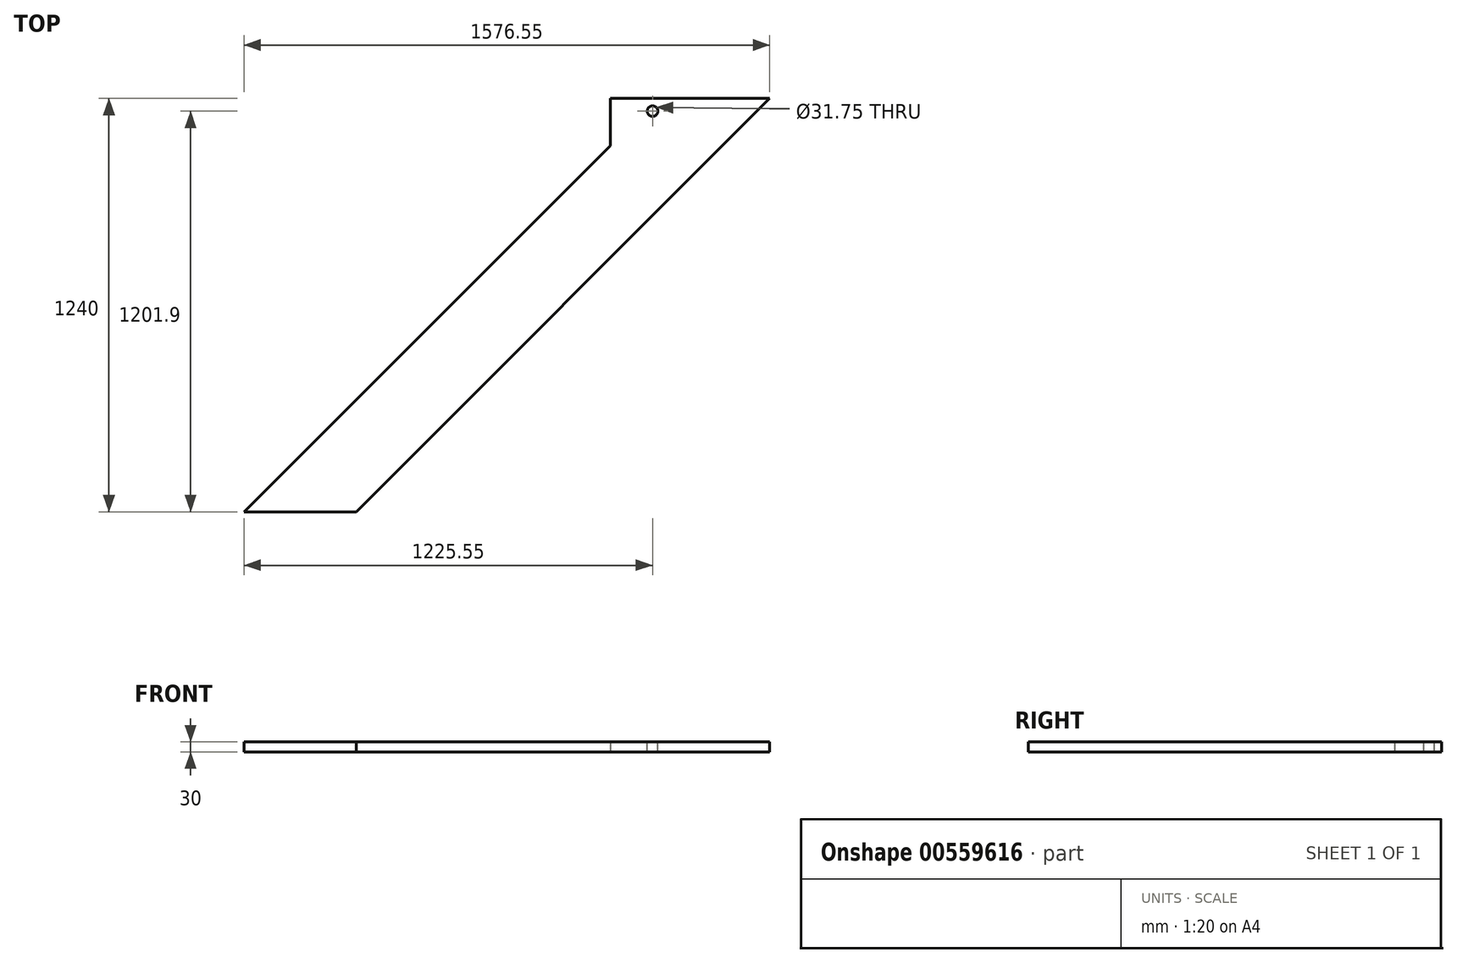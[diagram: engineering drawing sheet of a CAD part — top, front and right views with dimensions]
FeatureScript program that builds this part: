
annotation { "Feature Type Name" : "Feature", "Feature Type Description" : "" }
export const myFeature = defineFeature(function(context is Context, id is Id, definition is map)
    precondition{}
    {
        {
            var Q0;
            Q0=qCreatedBy(makeId("Top.planeOp"),FACE);
            var sketch = newSketch(context, id + "F0", { "sketchPlane" : qUnion([Q0])});
            skLineSegment(sketch, "E0.bottom", {"start": v(-635, 635) * mm, "end": v(635, 635) * mm, "construction": true});
            skLineSegment(sketch, "E0.top", {"start": v(-635, -635) * mm, "end": v(635, -635) * mm, "construction": true});
            skLineSegment(sketch, "E0.left", {"start": v(-635, 635) * mm, "end": v(-635, -635) * mm, "construction": true});
            skLineSegment(sketch, "E0.right", {"start": v(635, 605) * mm, "end": v(635, -635) * mm, "construction": true});
            skPoint(sketch, "E0.middle", {"position": v(0, 0) * mm});
            skLineSegment(sketch, "E1", {"start": v(-635, -635) * mm, "end": v(-463.55, -635) * mm, "construction": true});
            skLineSegment(sketch, "E2", {"start": v(-463.55, -635) * mm, "end": v(635, 463.55) * mm});
            skLineSegment(sketch, "E3", {"start": v(635, 463.55) * mm, "end": v(635, 605) * mm});
            skLineSegment(sketch, "E4", {"start": v(-463.55, -635) * mm, "end": v(-127, -635) * mm});
            skLineSegment(sketch, "E5", {"start": v(-127, -635) * mm, "end": v(1113, 605) * mm});
            skLineSegment(sketch, "E6", {"start": v(635, 635) * mm, "end": v(1143, 635) * mm, "construction": true});
            skLineSegment(sketch, "E7", {"start": v(635, 605) * mm, "end": v(1113, 605) * mm});
            skLineSegment(sketch, "E8", {"start": v(635, 635) * mm, "end": v(635, 605) * mm, "construction": true});
            skLineSegment(sketch, "E9", {"start": v(1143, 635) * mm, "end": v(1113, 605) * mm, "construction": true});
            skSolve(sketch);
        }
        {
            var Q0;
            Q0 = qSketchRegion(id + "F0", true);
            extrude(context, id + "F1", {"entities" : qUnion([Q0]), "depth" : 30 * mm, "offsetDistance" : 25.4 * mm});
        }
        {
            var Q0;
            Q0=makeQuery(id+"F1.opExtrude","CAP_FACE",FACE,{"disambiguationData":[OSD([sQuery(id+"F0.wireOp",EDGE,"E2"),sQuery(id+"F0.wireOp",EDGE,"E3"),sQuery(id+"F0.wireOp",EDGE,"E4"),sQuery(id+"F0.wireOp",EDGE,"E5"),sQuery(id+"F0.wireOp",EDGE,"E7")])],"isStart":false});
            var sketch = newSketch(context, id + "F2", { "sketchPlane" : qUnion([Q0])});
            skCircle(sketch, "E10", {"center": v(762, 566.9) * mm, "radius": 15.88 * mm});
            skSolve(sketch);
        }
        {
            var Q0;
            Q0 = qSketchRegion(id + "F2", true);
            extrude(context, id + "F3", {"entities" : qUnion([Q0]), "operationType" : NewBodyOperationType.REMOVE, "endBound" : BoundingType.UP_TO_NEXT, "oppositeDirection" : true, "depth" : 25.4 * mm, "offsetDistance" : 25.4 * mm});
        }
    });
